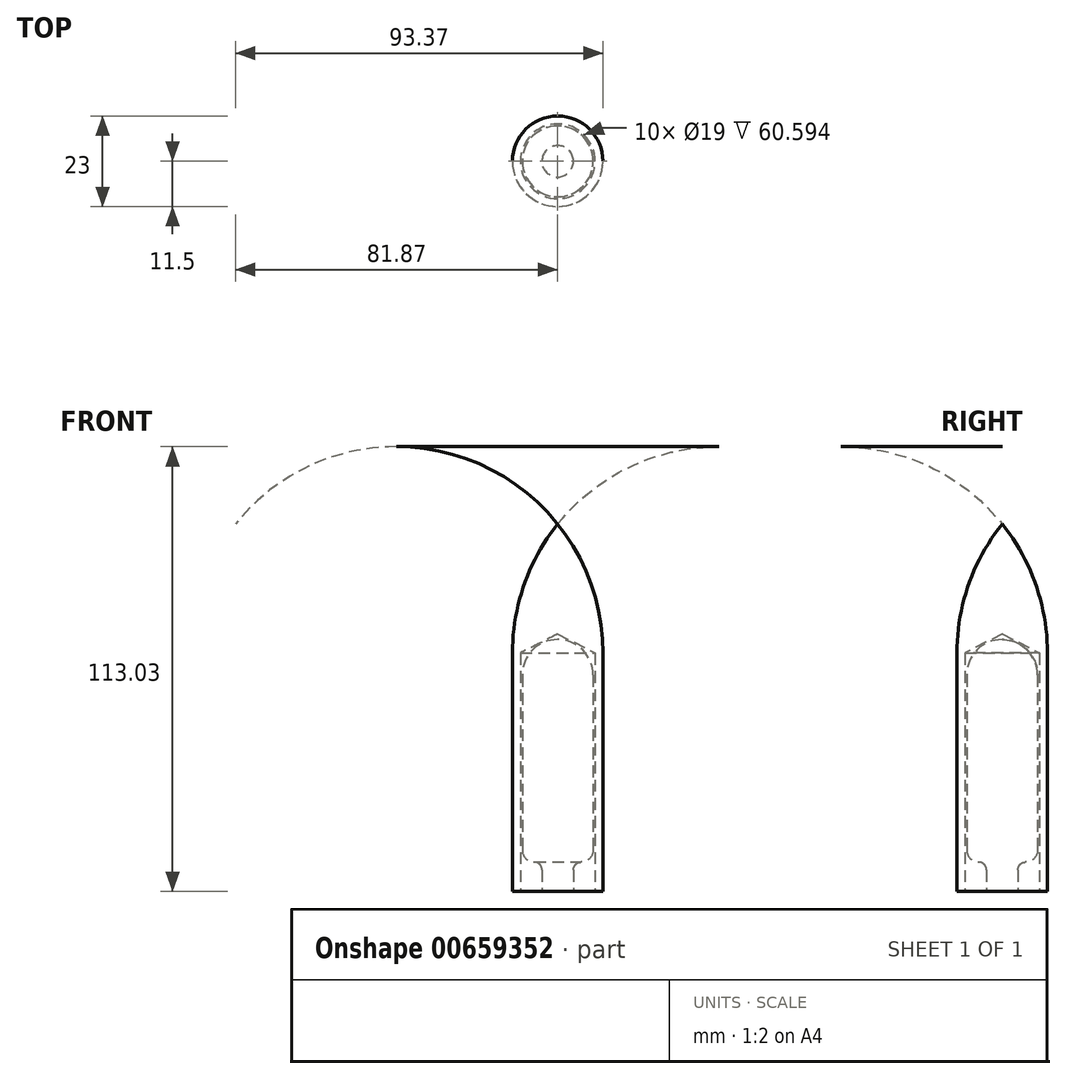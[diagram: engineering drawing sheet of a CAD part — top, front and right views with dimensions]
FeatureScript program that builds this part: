
annotation { "Feature Type Name" : "Feature", "Feature Type Description" : "" }
export const myFeature = defineFeature(function(context is Context, id is Id, definition is map)
    precondition{}
    {
        {
            var Q0;
            Q0=qCreatedBy(makeId("Right.planeOp"),FACE);
            var sketch = newSketch(context, id + "F0", { "sketchPlane" : qUnion([Q0])});
            skLineSegment(sketch, "E0", {"start": v(0, 0) * mm, "end": v(0, 64) * mm});
            skLineSegment(sketch, "E1", {"start": v(9, 10.54) * mm, "end": v(9, 55) * mm});
            skLineSegment(sketch, "E2", {"start": v(0, 0) * mm, "end": v(4, 0) * mm});
            skLineSegment(sketch, "E3", {"start": v(4, 0) * mm, "end": v(4, 5.5) * mm});
            skArc(sketch, "E4", {"start": v(9, 55) * mm, "mid": v(6.36, 61.36) * mm, "end": v(0, 64) * mm});
            skArc(sketch, "E5", {"start": v(5.94, 7.46) * mm, "mid": v(8.1, 8.37) * mm, "end": v(9, 10.54) * mm});
            skArc(sketch, "E6", {"start": v(5.94, 7.46) * mm, "mid": v(4.57, 6.89) * mm, "end": v(4, 5.5) * mm});
            skSolve(sketch);
        }
        {
            var Q0;
            Q0=makeQuery(id+"F0.imprint","IMPRINT",FACE,{"disambiguationData":[TD([[makeQuery(id+"F0.imprint","IMPRINT",EDGE,{"derivedFrom":sQuery(id+"F0.wireOp",EDGE,"E0")}),-1.0]])]});
            var Q1;
            Q1=sQuery(id+"F0.wireOp",EDGE,"E0");
            revolve(context, id + "F1", {"entities" : qUnion([Q0]), "axis" : qUnion([Q1]), "revolveType" : RevolveType.FULL});
        }
        {
            var Q0;
            Q0=qCreatedBy(makeId("Right.planeOp"),FACE);
            var sketch = newSketch(context, id + "F2", { "sketchPlane" : qUnion([Q0])});
            skLineSegment(sketch, "E7", {"start": v(0, 0) * mm, "end": v(0, 93.36) * mm});
            skLineSegment(sketch, "E8", {"start": v(11.5, 0) * mm, "end": v(11.5, 60.6) * mm});
            skLineSegment(sketch, "E9", {"start": v(0, 65.44) * mm, "end": v(9.5, 60.6) * mm});
            skLineSegment(sketch, "E10", {"start": v(9.5, 60.6) * mm, "end": v(9.5, 0) * mm});
            skLineSegment(sketch, "E11", {"start": v(9.5, 0) * mm, "end": v(11.5, 0) * mm});
            skArc(sketch, "E12", {"start": v(11.5, 60.6) * mm, "mid": v(8.54, 77.96) * mm, "end": v(0, 93.36) * mm});
            skSolve(sketch);
        }
        {
            var Q0;
            Q0=makeQuery(id+"F2.imprint","IMPRINT",FACE,{"disambiguationData":[TD([[makeQuery(id+"F2.imprint","IMPRINT",EDGE,{"derivedFrom":sQuery(id+"F2.wireOp",EDGE,"E8")}),1.0]])]});
            var Q1;
            Q1=sQuery(id+"F2.wireOp",EDGE,"E7");
            revolve(context, id + "F3", {"entities" : qUnion([Q0]), "axis" : qUnion([Q1]), "revolveType" : RevolveType.FULL});
        }
    });
